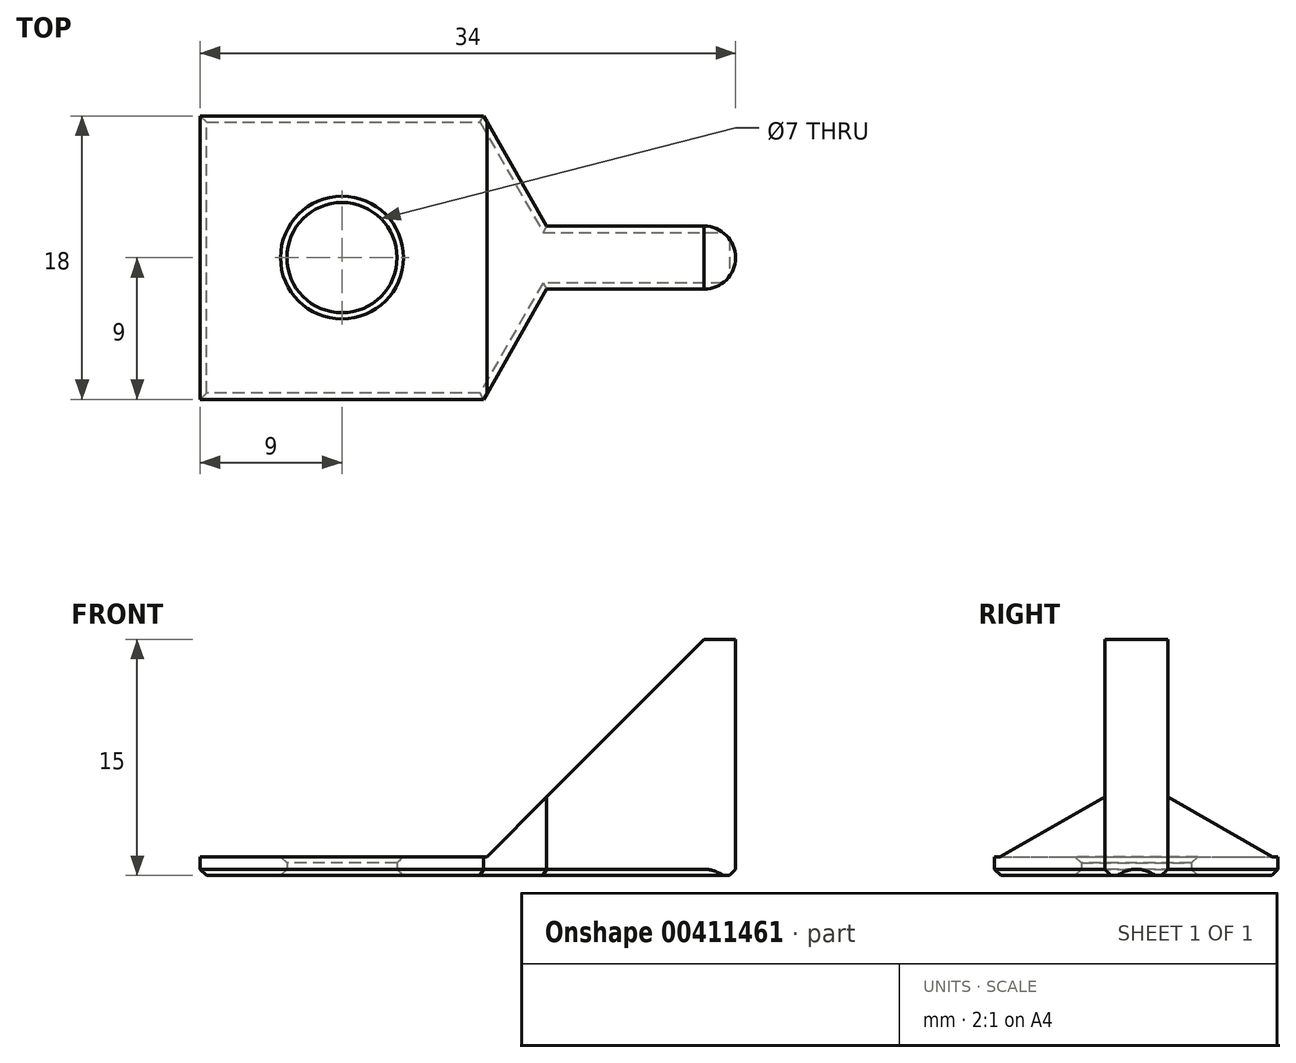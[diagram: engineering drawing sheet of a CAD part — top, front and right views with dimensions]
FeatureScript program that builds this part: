
annotation { "Feature Type Name" : "Feature", "Feature Type Description" : "" }
export const myFeature = defineFeature(function(context is Context, id is Id, definition is map)
    precondition{}
    {
        {
            var Q0;
            Q0=qCreatedBy(makeId("Top.planeOp"),FACE);
            var sketch = newSketch(context, id + "F0", { "sketchPlane" : qUnion([Q0])});
            skCircle(sketch, "E0", {"center": v(0, 0) * mm, "radius": 3.5 * mm});
            skLineSegment(sketch, "E1.bottom", {"start": v(9, -9) * mm, "end": v(-9, -9) * mm});
            skLineSegment(sketch, "E1.top", {"start": v(9, 9) * mm, "end": v(-9, 9) * mm});
            skLineSegment(sketch, "E1.left", {"start": v(9, -9) * mm, "end": v(9, 9) * mm});
            skLineSegment(sketch, "E1.right", {"start": v(-9, -9) * mm, "end": v(-9, 9) * mm});
            skSolve(sketch);
        }
        {
            var Q0;
            Q0 = qSketchRegion(id + "F0", true);
            extrude(context, id + "F1", {"entities" : qUnion([Q0]), "depth" : 1.2 * mm, "offsetDistance" : 25 * mm});
        }
        {
            var Q0;
            Q0=makeQuery(id+"F1.opExtrude","CAP_FACE",FACE,{"disambiguationData":[OSD([sQuery(id+"F0.wireOp",EDGE,"E0"),sQuery(id+"F0.wireOp",EDGE,"E1.bottom"),sQuery(id+"F0.wireOp",EDGE,"E1.top"),sQuery(id+"F0.wireOp",EDGE,"E1.left"),sQuery(id+"F0.wireOp",EDGE,"E1.right")])],"isStart":true});
            var sketch = newSketch(context, id + "F2", { "sketchPlane" : qUnion([Q0])});
            skLineSegment(sketch, "E2", {"start": v(9, -9) * mm, "end": v(13, -2) * mm});
            skLineSegment(sketch, "E3", {"start": v(13, -2) * mm, "end": v(25, -2) * mm});
            skLineSegment(sketch, "E4", {"start": v(25, -2) * mm, "end": v(25, 0) * mm});
            skLineSegment(sketch, "E5", {"start": v(25, 0) * mm, "end": v(9, 0) * mm});
            skLineSegment(sketch, "E6", {"start": v(9, 0) * mm, "end": v(9, -9) * mm});
            skLineSegment(sketch, "E7.MirrorCS", {"start": v(9, 9) * mm, "end": v(13, 2) * mm});
            skLineSegment(sketch, "E8.MirrorCS", {"start": v(13, 2) * mm, "end": v(25, 2) * mm});
            skLineSegment(sketch, "E9.MirrorCS", {"start": v(25, 2) * mm, "end": v(25, 0) * mm});
            skLineSegment(sketch, "E10.MirrorCS", {"start": v(9, 0) * mm, "end": v(9, 9) * mm});
            skSolve(sketch);
        }
        {
            var Q0;
            Q0 = qSketchRegion(id + "F2", true);
            extrude(context, id + "F3", {"entities" : qUnion([Q0]), "operationType" : NewBodyOperationType.ADD, "oppositeDirection" : true, "depth" : 15 * mm, "offsetDistance" : 25 * mm});
        }
        {
            var Q0;
            Q0=makeQuery(id+"F3.opExtrude","CAP_EDGE",EDGE,{"disambiguationData":[OSD([sQuery(id+"F2.wireOp",EDGE,"E6"),sQuery(id+"F2.wireOp",EDGE,"E10.MirrorCS")])],"isStart":false});
            chamfer(context, id + "F4", {"entities" : qUnion([Q0]), "width" : 14 * mm, "tangentPropagation" : true});
        }
        {
            var Q0;
            Q0=makeQuery(id+"F3.boolean.opBoolean","MERGE",FACE,{"derivedFrom":[makeQuery(id+"F1.opExtrude","CAP_FACE",FACE,{"disambiguationData":[OSD([sQuery(id+"F0.wireOp",EDGE,"E0"),sQuery(id+"F0.wireOp",EDGE,"E1.bottom"),sQuery(id+"F0.wireOp",EDGE,"E1.top"),sQuery(id+"F0.wireOp",EDGE,"E1.left"),sQuery(id+"F0.wireOp",EDGE,"E1.right")])],"isStart":true}),makeQuery(id+"F3.opExtrude","CAP_FACE",FACE,{"disambiguationData":[OSD([sQuery(id+"F2.wireOp",EDGE,"E2"),sQuery(id+"F2.wireOp",EDGE,"E3"),sQuery(id+"F2.wireOp",EDGE,"E4"),sQuery(id+"F2.wireOp",EDGE,"E6"),sQuery(id+"F2.wireOp",EDGE,"E7.MirrorCS"),sQuery(id+"F2.wireOp",EDGE,"E8.MirrorCS"),sQuery(id+"F2.wireOp",EDGE,"E9.MirrorCS"),sQuery(id+"F2.wireOp",EDGE,"E10.MirrorCS")])],"isStart":true})]});
            var Q1;
            Q1=makeQuery(id+"F1.opExtrude","CAP_EDGE",EDGE,{"disambiguationData":[OSD([sQuery(id+"F0.wireOp",EDGE,"E0")])],"isStart":false});
            chamfer(context, id + "F5", {"entities" : qUnion([Q0, Q1]), "width" : .4 * mm, "tangentPropagation" : true});
        }
        {
            var Q0;
            Q0=makeQuery(id+"F3.opExtrude","SWEPT_EDGE",EDGE,{"disambiguationData":[OSD([sQuery(id+"F2.wireOp",EDGE,"E8.MirrorCS"),sQuery(id+"F2.wireOp",EDGE,"E9.MirrorCS")])]});
            var Q1;
            Q1=makeQuery(id+"F3.opExtrude","SWEPT_EDGE",EDGE,{"disambiguationData":[OSD([sQuery(id+"F2.wireOp",EDGE,"E3"),sQuery(id+"F2.wireOp",EDGE,"E4")])]});
            fillet(context, id + "F6", {"entities" : qUnion([Q0, Q1]), "tangentPropagation" : true, "radius" : 2 * mm, "defaultsChanged" : false, "vertexSettings" : [], "allowEdgeOverflow" : false});
        }
    });
